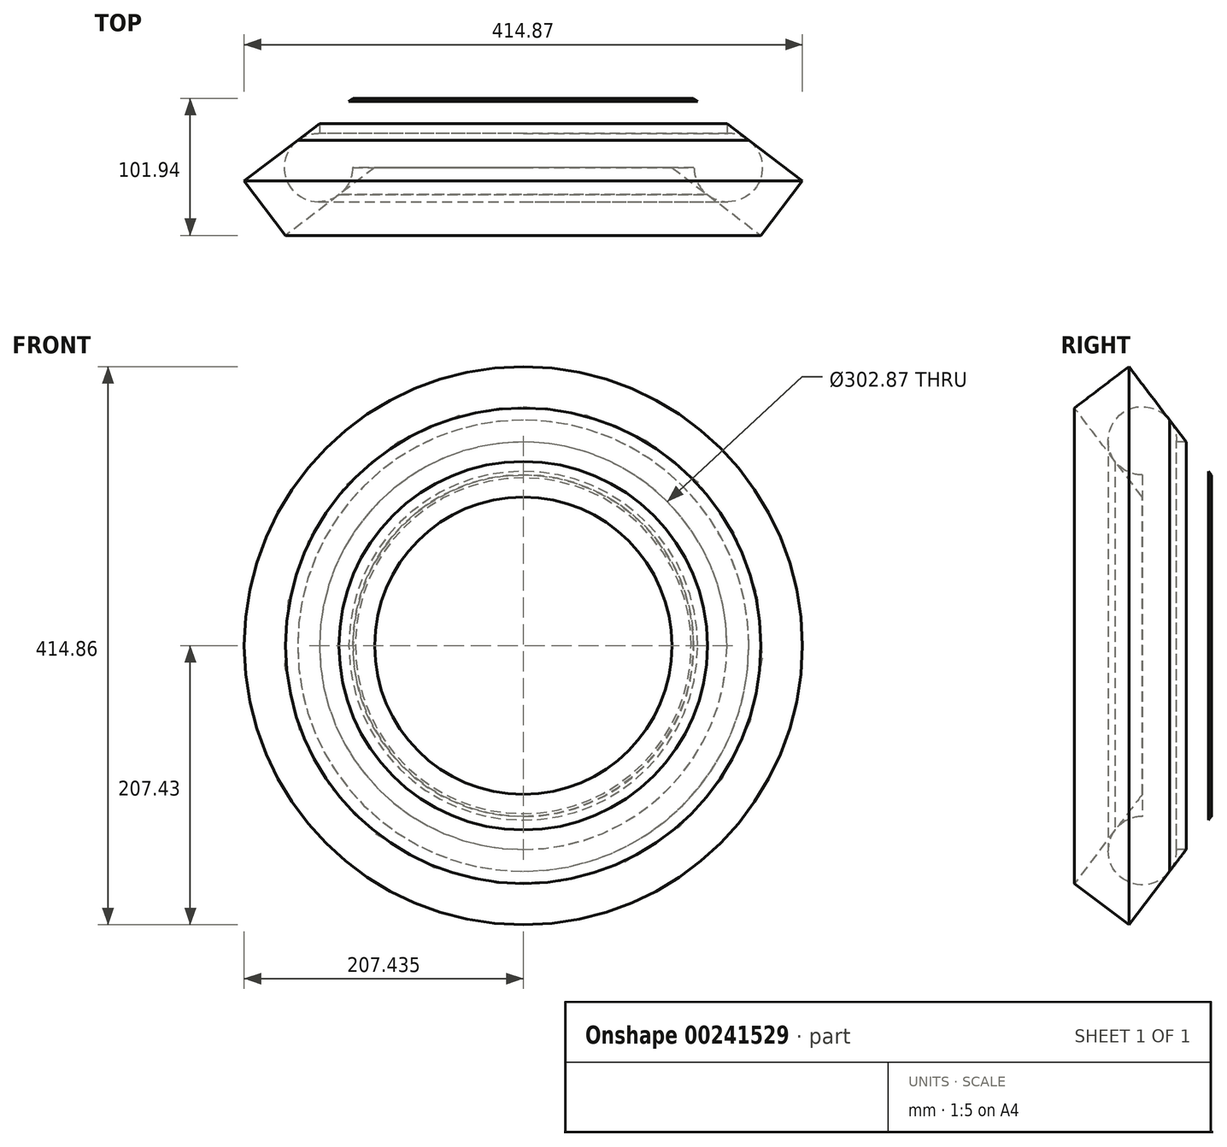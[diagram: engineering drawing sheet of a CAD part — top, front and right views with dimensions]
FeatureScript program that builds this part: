
annotation { "Feature Type Name" : "Feature", "Feature Type Description" : "" }
export const myFeature = defineFeature(function(context is Context, id is Id, definition is map)
    precondition{}
    {
        {
            var Q0;
            Q0=qCreatedBy(makeId("Top.planeOp"),FACE);
            var sketch = newSketch(context, id + "F0", { "sketchPlane" : qUnion([Q0])});
            skLineSegment(sketch, "E0.bottom", {"start": v(25.24, -50.34) * mm, "end": v(-55.62, 11.16) * mm});
            skLineSegment(sketch, "E0.top", {"start": v(56, -9.91) * mm, "end": v(-24.87, 51.6) * mm});
            skLineSegment(sketch, "E0.left", {"start": v(25.24, -50.34) * mm, "end": v(56, -9.91) * mm});
            skLineSegment(sketch, "E0.right", {"start": v(-55.62, 11.16) * mm, "end": v(-24.87, 51.6) * mm});
            skCircle(sketch, "E1", {"center": v(0.89, 0.1) * mm, "radius": 25.4 * mm});
            skSolve(sketch);
        }
        {
            var Q0;
            Q0=qCreatedBy(makeId("Front.planeOp"),FACE);
            var sketch = newSketch(context, id + "F1", { "sketchPlane" : qUnion([Q0])});
            skCircle(sketch, "E2", {"center": v(-151.43, 0) * mm, "radius": 151.43 * mm});
            skSolve(sketch);
        }
        {
            var Q0;
            {var subQ0=sQuery(id+"F0.wireOp",EDGE,"E0.left");Q0=makeQuery(id+"F0.imprint","IMPRINT",FACE,{"disambiguationData":[TD([[makeQuery(id+"F0.imprint","IMPRINT",EDGE,{"derivedFrom":subQ0}),1.0]])]});}
            var Q1;
            {var subQ0=sQuery(id+"F0.wireOp",EDGE,"E0.right");Q1=makeQuery(id+"F0.imprint","IMPRINT",FACE,{"disambiguationData":[TD([[makeQuery(id+"F0.imprint","IMPRINT",EDGE,{"derivedFrom":subQ0}),-1.0]])]});}
            var Q2;
            Q2=sQuery(id+"F1.wireOp",EDGE,"E2");
            revolve(context, id + "F2", {"entities" : qUnion([Q0, Q1]), "axis" : qUnion([Q2]), "revolveType" : RevolveType.FULL});
        }
        {
            var Q0;
            Q0=makeQuery(id+"F1.imprint","IMPRINT",FACE,{"disambiguationData":[TD([[makeQuery(id+"F1.imprint","IMPRINT",EDGE,{"derivedFrom":sQuery(id+"F1.wireOp",EDGE,"E2")}),1.0]])]});
            extrude(context, id + "F3", {"entities" : qUnion([Q0]), "operationType" : NewBodyOperationType.REMOVE, "oppositeDirection" : true, "depth" : 25.4 * mm});
        }
        {
            var Q0;
            Q0=makeQuery(id+"F1.imprint","IMPRINT",FACE,{"disambiguationData":[TD([[makeQuery(id+"F1.imprint","IMPRINT",EDGE,{"derivedFrom":sQuery(id+"F1.wireOp",EDGE,"E2")}),1.0]])]});
            extrude(context, id + "F4", {"entities" : qUnion([Q0]), "operationType" : NewBodyOperationType.REMOVE, "oppositeDirection" : true, "depth" : 49.28 * mm});
        }
    });
